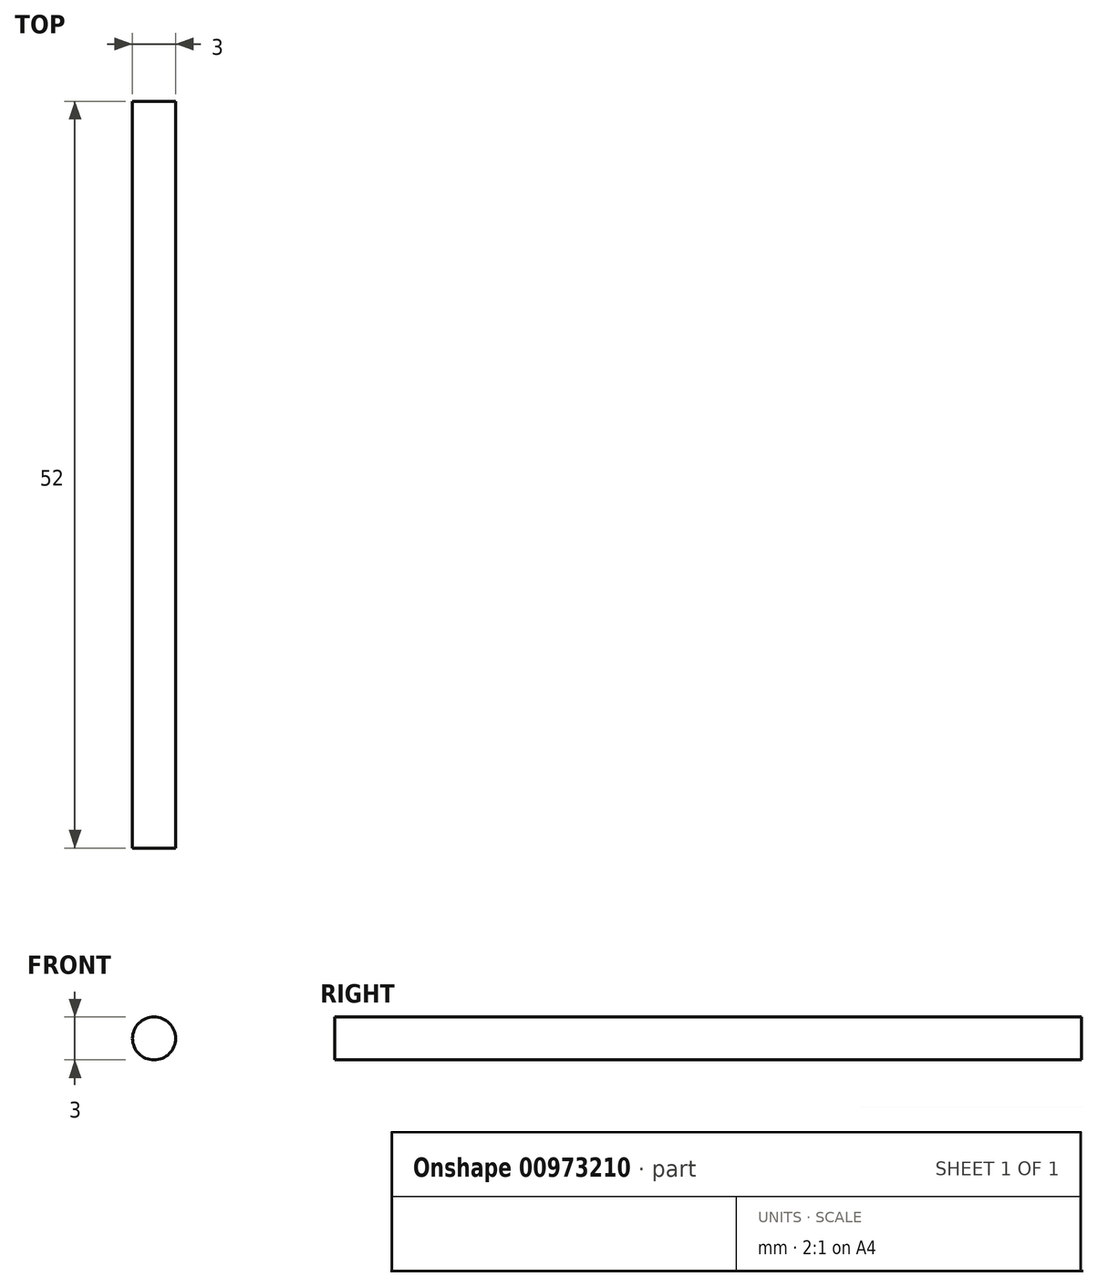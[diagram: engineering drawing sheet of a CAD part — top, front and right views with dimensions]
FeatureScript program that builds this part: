
annotation { "Feature Type Name" : "Feature", "Feature Type Description" : "" }
export const myFeature = defineFeature(function(context is Context, id is Id, definition is map)
    precondition{}
    {
        {
            var Q0;
            Q0=qCreatedBy(makeId("Front.planeOp"),FACE);
            var sketch = newSketch(context, id + "F0", { "sketchPlane" : qUnion([Q0])});
            skCircle(sketch, "E0", {"center": v(0, 0) * mm, "radius": 1.5 * mm});
            skSolve(sketch);
        }
        {
            var Q0;
            Q0 = qSketchRegion(id + "F0", true);
            extrude(context, id + "F1", {"entities" : qUnion([Q0]), "depth" : 52 * mm, "offsetDistance" : 25 * mm});
        }
    });
